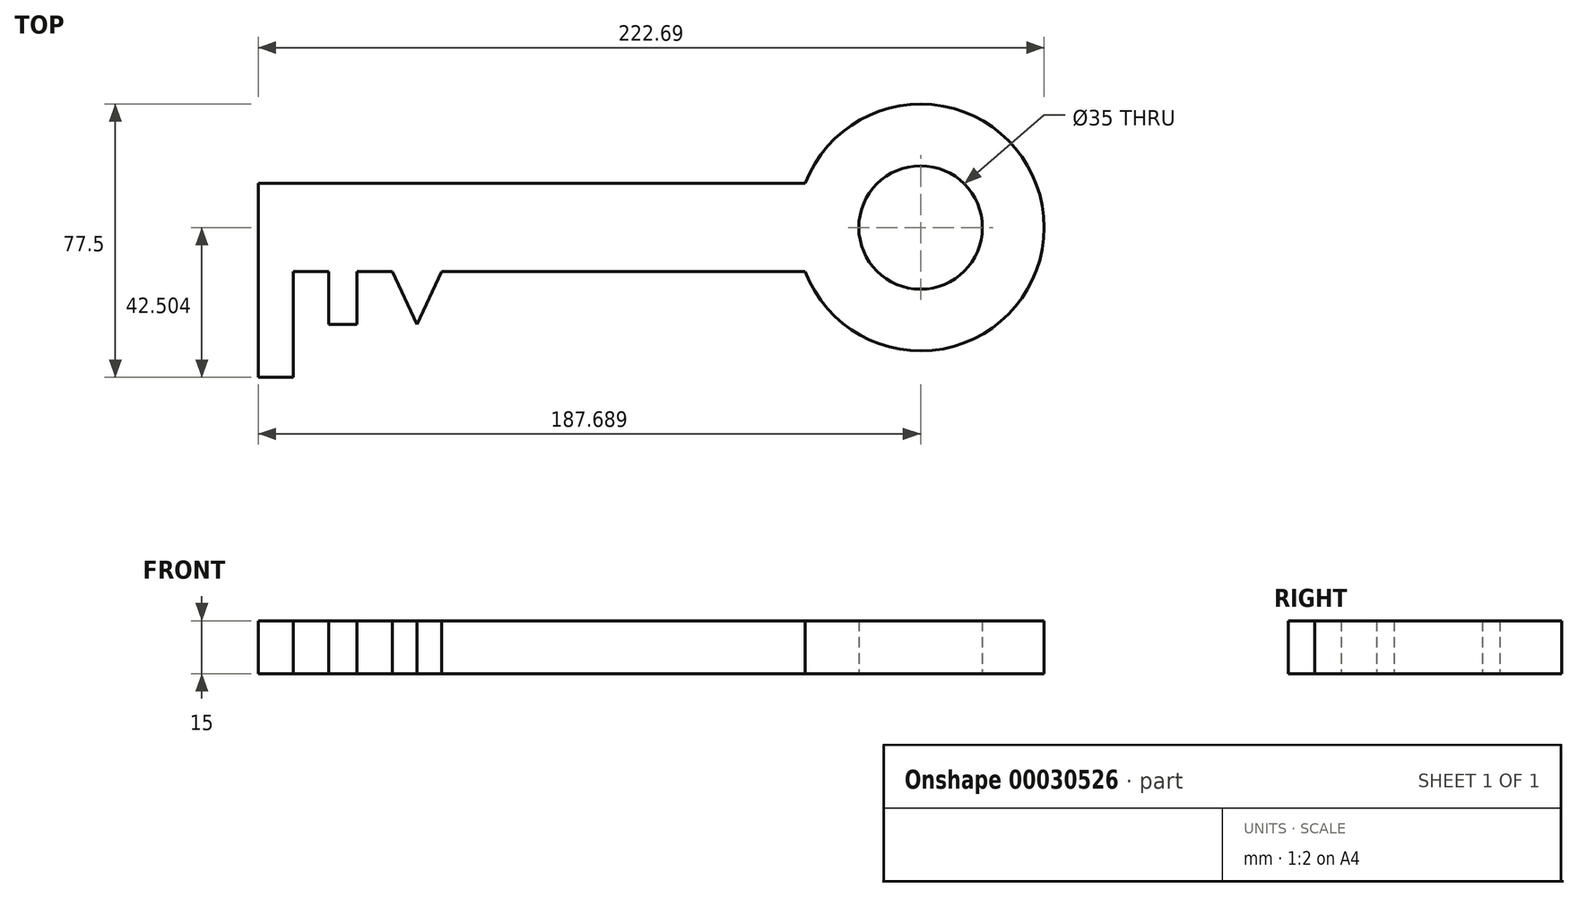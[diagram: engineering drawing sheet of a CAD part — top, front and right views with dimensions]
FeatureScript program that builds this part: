
annotation { "Feature Type Name" : "Feature", "Feature Type Description" : "" }
export const myFeature = defineFeature(function(context is Context, id is Id, definition is map)
    precondition{}
    {
        {
            var Q0;
            Q0=qCreatedBy(makeId("Top.planeOp"),FACE);
            var sketch = newSketch(context, id + "F0", { "sketchPlane" : qUnion([Q0])});
            skLineSegment(sketch, "E0.bottom", {"start": v(-117.71, -11.65) * mm, "end": v(37.29, -11.65) * mm});
            skLineSegment(sketch, "E0.top", {"start": v(-107.71, -36.65) * mm, "end": v(-79.71, -36.65) * mm});
            skLineSegment(sketch, "E0.left", {"start": v(-117.71, -11.65) * mm, "end": v(-117.71, -36.65) * mm});
            skLineSegment(sketch, "E1.top", {"start": v(-117.71, -66.65) * mm, "end": v(-107.71, -66.65) * mm});
            skLineSegment(sketch, "E1.left", {"start": v(-117.71, -36.65) * mm, "end": v(-117.71, -66.65) * mm});
            skLineSegment(sketch, "E1.right", {"start": v(-107.71, -36.65) * mm, "end": v(-107.71, -66.65) * mm});
            skLineSegment(sketch, "E2.top", {"start": v(-97.71, -51.65) * mm, "end": v(-89.71, -51.65) * mm});
            skLineSegment(sketch, "E2.left", {"start": v(-97.71, -36.65) * mm, "end": v(-97.71, -51.65) * mm});
            skLineSegment(sketch, "E2.right", {"start": v(-89.71, -36.65) * mm, "end": v(-89.71, -51.65) * mm});
            skLineSegment(sketch, "E3", {"start": v(-79.71, -36.65) * mm, "end": v(-72.71, -51.65) * mm});
            skLineSegment(sketch, "E4", {"start": v(-72.71, -51.65) * mm, "end": v(-65.71, -36.65) * mm});
            skArc(sketch, "E5", {"start": v(37.29, -36.65) * mm, "mid": v(104.98, -24.15) * mm, "end": v(37.29, -11.65) * mm});
            skCircle(sketch, "E6", {"center": v(69.98, -24.15) * mm, "radius": 17.5 * mm});
            skLineSegment(sketch, "E7", {"start": v(-117.71, -24.15) * mm, "end": v(69.98, -24.15) * mm, "construction": true});
            skLineSegment(sketch, "E8.trimOffspring", {"start": v(-65.71, -36.65) * mm, "end": v(37.29, -36.65) * mm});
            skSolve(sketch);
        }
        {
            var Q0;
            Q0=makeQuery(id+"F0.imprint","IMPRINT",FACE,{"disambiguationData":[TD([[makeQuery(id+"F0.imprint","IMPRINT",EDGE,{"derivedFrom":sQuery(id+"F0.wireOp",EDGE,"E0.bottom")}),-1.0]])]});
            var Q1;
            Q1=makeQuery(id+"F0.imprint","IMPRINT",FACE,{"disambiguationData":[TD([[makeQuery(id+"F0.imprint","IMPRINT",EDGE,{"derivedFrom":sQuery(id+"F0.wireOp",EDGE,"E2.top")}),1.0]])]});
            extrude(context, id + "F1", {"entities" : qUnion([Q0, Q1]), "depth" : 15 * mm});
        }
    });
